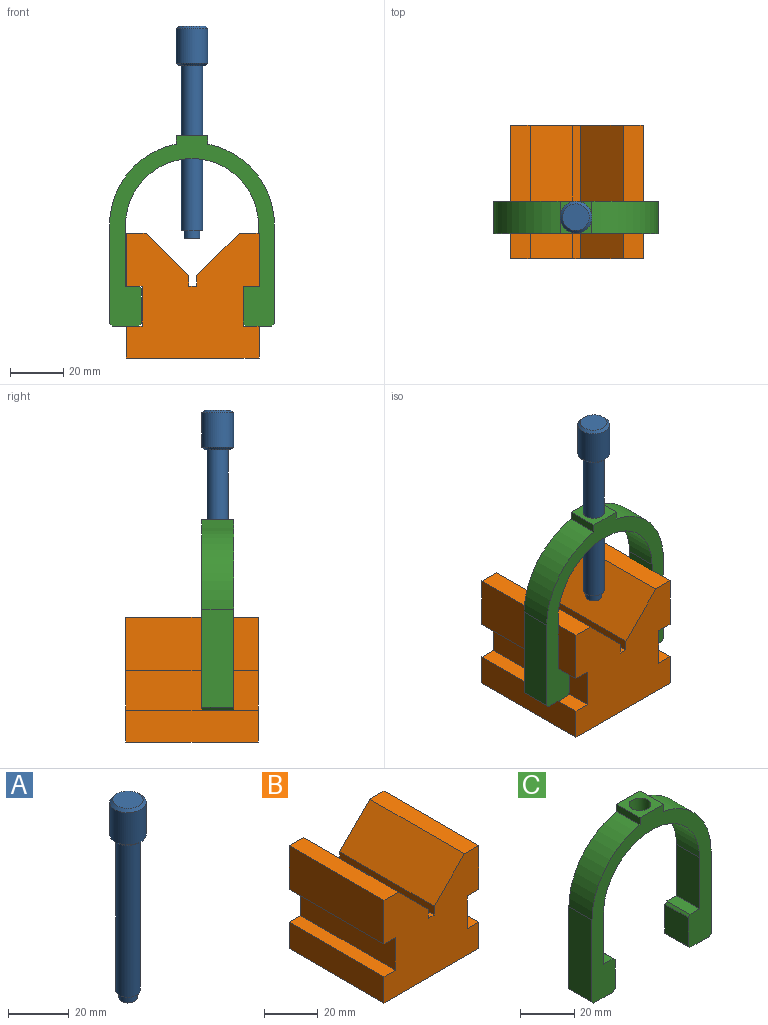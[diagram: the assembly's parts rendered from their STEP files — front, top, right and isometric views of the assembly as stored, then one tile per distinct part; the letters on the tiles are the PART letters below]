
ASSEMBLY  parts=3 mates=2
PART A: 9 faces, bbox 12x12x80 mm
  f0: cylinder r=4mm len=62mm, axis (0,0,-1), area 1558.2mm2, adj f1,f4
  f1: plane 8x8mm, normal (0,0,-1), area 22mm2, adj f0,f5
  f2: cylinder r=6mm len=13mm, axis (0,0,-1), area 490.1mm2, adj f7,f8
  f3: plane 10x10mm, normal (0,0,1), area 78.5mm2, adj f7
  f4: plane 10x10mm, normal (0,0,-1), area 28.3mm2, adj f0,f8
  f5: cylinder r=3mm len=6mm, axis (0,0,1), area 56.5mm2, adj f1,f6
  f6: plane 6x6mm, normal (0,0,-1), area 28.3mm2, adj f5
  f7: cone r=5mm half-angle=45deg, axis (0,0,-1), area 48.9mm2, adj f2,f3
  f8: cone r=6mm half-angle=45deg, axis (0,0,1), area 48.9mm2, adj f2,f4
PART B: 20 faces, bbox 50x50x47 mm
  f0: plane 50x7.5mm, normal (0,0,1), area 375mm2, adj f1,f17,f18,f19
  f1: plane 50x16mm, normal (-0.71,0,0.71), area 1131.3mm2, adj f0,f2,f18,f19
  f2: plane 50x4mm, normal (-1,0,0), area 200mm2, adj f1,f3,f18,f19
  f3: plane 50x3mm, normal (0,0,1), area 150mm2, adj f2,f4,f18,f19
  f4: plane 50x4mm, normal (1,0,0), area 200mm2, adj f3,f5,f18,f19
  f5: plane 50x16mm, normal (0.71,0,0.71), area 1131.4mm2, adj f4,f6,f18,f19
  f6: plane 50x7.5mm, normal (0,0,1), area 375mm2, adj f5,f7,f18,f19
  f7: plane 50x20mm, normal (-1,0,0), area 1000mm2, adj f6,f8,f18,f19
  f8: plane 50x6mm, normal (0,0,-1), area 300mm2, adj f7,f9,f18,f19
  f9: plane 50x15mm, normal (-1,0,0), area 750mm2, adj f8,f10,f18,f19
  f10: plane 50x6mm, normal (0,0,1), area 300mm2, adj f9,f11,f18,f19
  f11: plane 50x12mm, normal (-1,0,0), area 600mm2, adj f10,f12,f18,f19
  f12: plane 50x50mm, normal (0,0,-1), area 2500mm2, adj f11,f13,f18,f19
  f13: plane 50x12mm, normal (1,0,0), area 600mm2, adj f12,f14,f18,f19
  f14: plane 50x6mm, normal (0,0,1), area 300mm2, adj f13,f15,f18,f19
  f15: plane 50x15mm, normal (1,0,0), area 750mm2, adj f14,f16,f18,f19
  f16: plane 50x6mm, normal (0,0,-1), area 300mm2, adj f15,f17,f18,f19
  f17: plane 50x20mm, normal (1,0,0), area 1000mm2, adj f0,f16,f18,f19
  f18: plane 50x47mm, normal (0,-1,0), area 1854mm2, adj f0,f1,f2,f3,f4,f5,f6,f7
  f19: plane 50x47mm, normal (0,1,0), area 1854mm2, adj f0,f1,f2,f3,f4,f5,f6,f7
PART C: 25 faces, bbox 62x12x71.6 mm
  f0: cylinder r=31mm len=30.41mm, axis (0,-1,0), area 511.9mm2, adj f11,f12,f13,f17
  f1: cylinder r=4mm len=8.91mm, axis (0,0,1), area 219.8mm2, adj f3,f18
  f2: cylinder r=31mm len=30.41mm, axis (0,-1,0), area 511.9mm2, adj f11,f13,f14,f16
  f3: cylinder r=25mm len=50mm, axis (0,-1,0), area 892mm2, adj f1,f4,f9,f11,f13
  f4: plane 23x12mm, normal (1,0,0), area 276mm2, adj f3,f5,f11,f13
  f5: plane 12x5mm, normal (0,0,1), area 60mm2, adj f4,f11,f13,f24
  f6: plane 13x12mm, normal (1,0,0), area 156mm2, adj f11,f13,f23,f24
  f7: plane 13x12mm, normal (-1,0,0), area 156mm2, adj f11,f13,f20,f21
  f8: plane 12x5mm, normal (0,0,1), area 60mm2, adj f9,f11,f13,f20
  f9: plane 23x12mm, normal (-1,0,0), area 276mm2, adj f3,f8,f11,f13
  f10: plane 12x10mm, normal (0,0,-1), area 120mm2, adj f11,f13,f21,f22
  f11: plane 71.59x62mm, normal (0,-1,0), area 1194.2mm2, adj f0,f2,f3,f4,f5,f6,f7,f8
  f12: plane 37x12mm, normal (1,0,0), area 444mm2, adj f0,f11,f13,f22
  f13: plane 71.59x62mm, normal (0,1,0), area 1194.2mm2, adj f0,f2,f3,f4,f5,f6,f7,f8
  f14: plane 37x12mm, normal (-1,0,0), area 444mm2, adj f2,f11,f13,f19
  f15: plane 12x10mm, normal (0,0,-1), area 120mm2, adj f11,f13,f19,f23
  f16: plane 12x3.17mm, normal (-1,0,0), area 38.1mm2, adj f2,f11,f13,f18
  f17: plane 12x3.17mm, normal (1,0,0), area 38.1mm2, adj f0,f11,f13,f18
  f18: plane 12x12mm, normal (0,0,1), area 93.7mm2, adj f1,f11,f13,f16,f17
  f19: plane 12x1mm, normal (-0.71,0,-0.71), area 17mm2, adj f11,f13,f14,f15
  f20: plane 12x1mm, normal (-0.71,0,0.71), area 17mm2, adj f7,f8,f11,f13
  f21: plane 12x1mm, normal (-0.71,0,-0.71), area 17mm2, adj f7,f10,f11,f13
  f22: plane 12x1mm, normal (0.71,0,-0.71), area 17mm2, adj f10,f11,f12,f13
  f23: plane 12x1mm, normal (0.71,0,-0.71), area 17mm2, adj f6,f11,f13,f15
  f24: plane 12x1mm, normal (0.71,0,0.71), area 17mm2, adj f5,f6,f11,f13
PLACE A rot(axis=(0,0,1),0deg) t=(20.48,-44.61,30.84)mm
PLACE B t=(-4.28,-9.94,-15.45)mm fixed
PLACE C t=(20.48,-44.61,66.55)mm
MATE parallel C.f6 <-> B.f9  axis (1,0,0) through (1.48,-44.61,4.05)mm
MATE cylindrical A.f0 <-> C.f1  axis (0,0,-1) through (20.48,-44.61,63.42)mm
